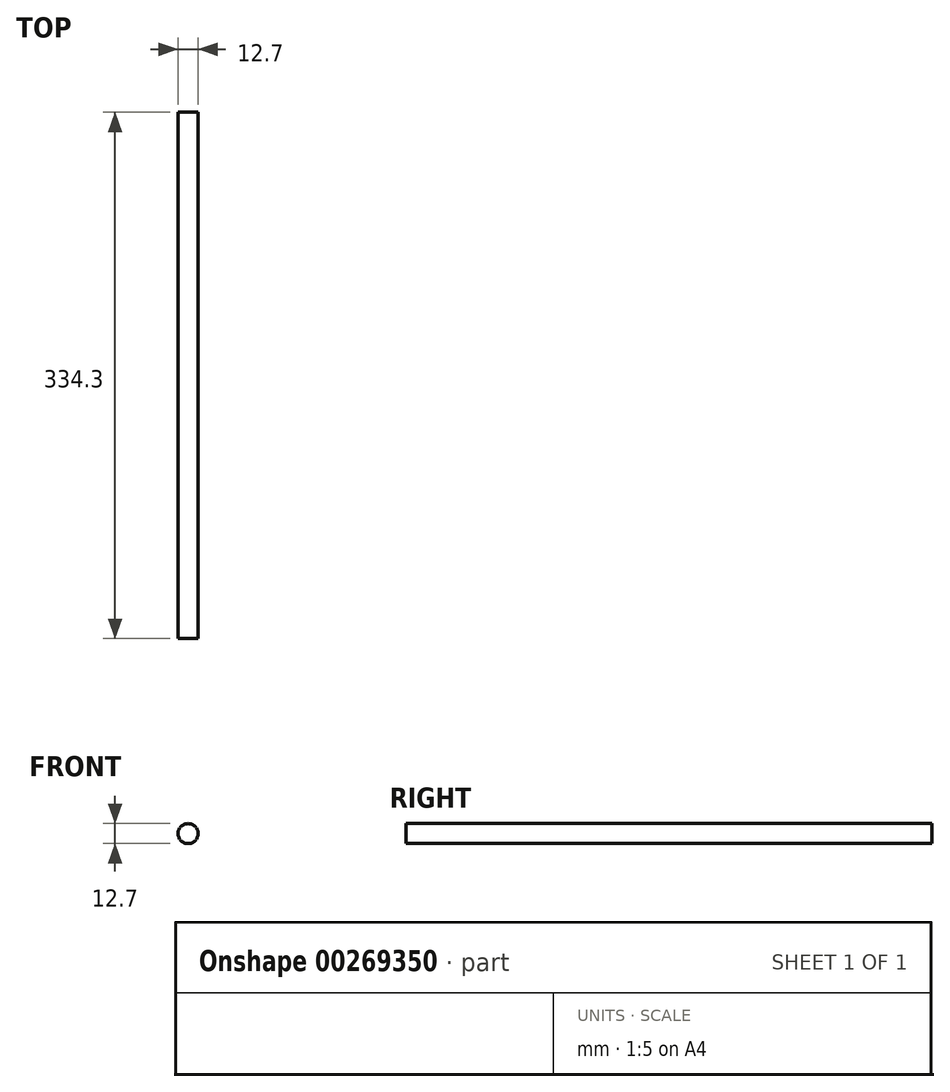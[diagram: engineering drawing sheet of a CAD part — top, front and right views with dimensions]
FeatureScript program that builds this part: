
annotation { "Feature Type Name" : "Feature", "Feature Type Description" : "" }
export const myFeature = defineFeature(function(context is Context, id is Id, definition is map)
    precondition{}
    {
        {
            var Q0;
            Q0=qCreatedBy(makeId("Front.planeOp"),FACE);
            var sketch = newSketch(context, id + "F0", { "sketchPlane" : qUnion([Q0])});
            skCircle(sketch, "E0", {"center": v(0, 0) * mm, "radius": 6.35 * mm});
            skSolve(sketch);
        }
        {
            var Q0;
            Q0=makeQuery(id+"F0.imprint","IMPRINT",FACE,{"disambiguationData":[TD([[makeQuery(id+"F0.imprint","IMPRINT",EDGE,{"derivedFrom":sQuery(id+"F0.wireOp",EDGE,"E0")}),1.0]])]});
            extrude(context, id + "F1", {"entities" : qUnion([Q0]), "depth" : 334.3 * mm});
        }
    });
